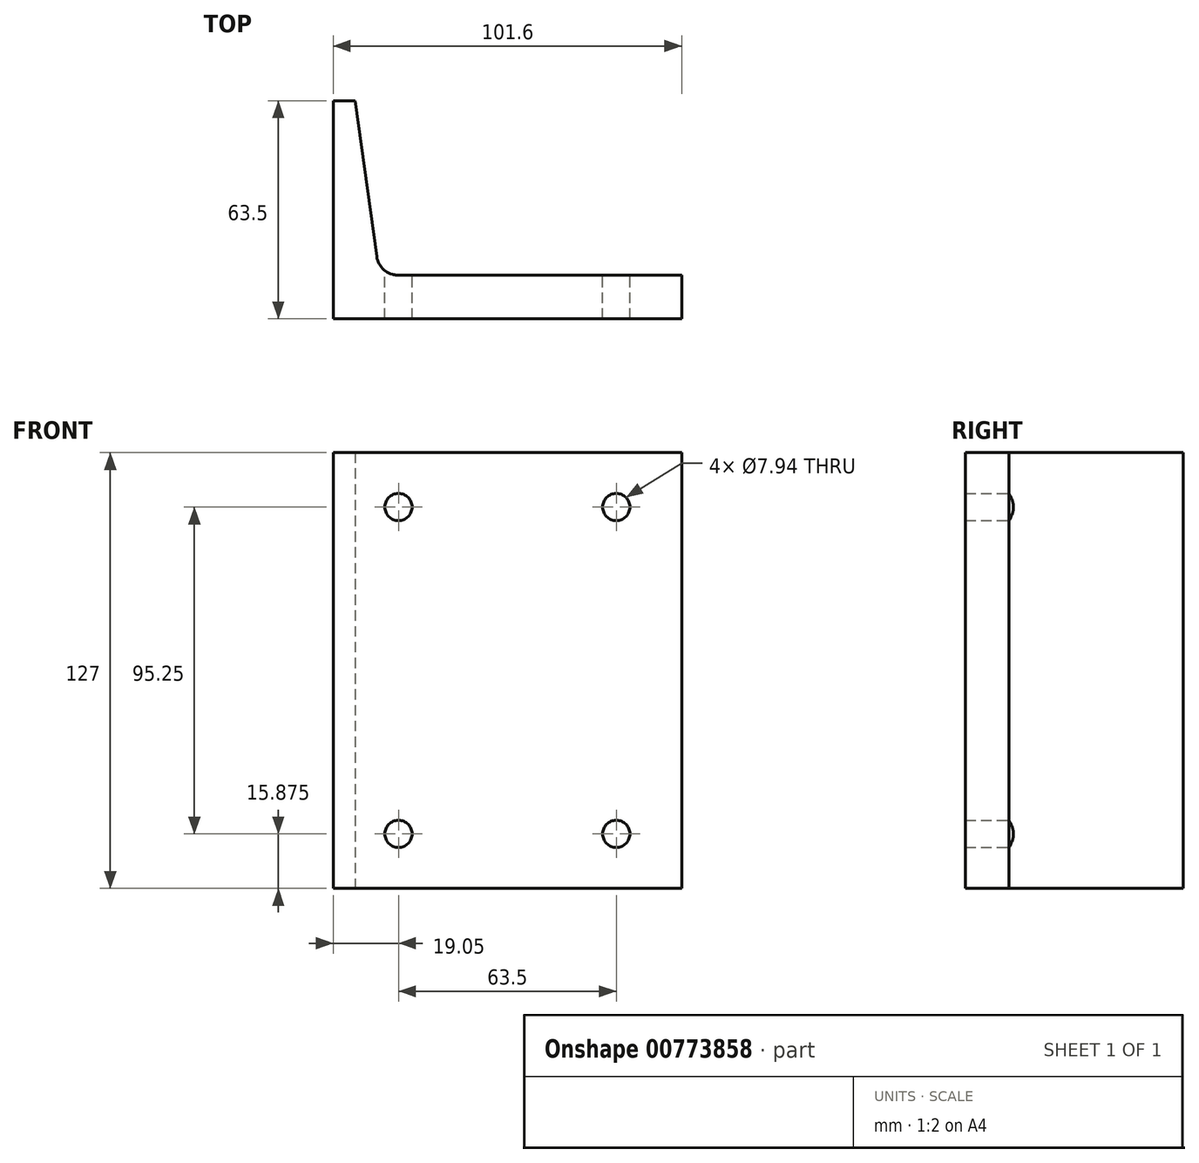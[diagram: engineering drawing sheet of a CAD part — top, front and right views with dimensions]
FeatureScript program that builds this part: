
annotation { "Feature Type Name" : "Feature", "Feature Type Description" : "" }
export const myFeature = defineFeature(function(context is Context, id is Id, definition is map)
    precondition{}
    {
        {
            var Q0;
            Q0=qCreatedBy(makeId("Top.planeOp"),FACE);
            var sketch = newSketch(context, id + "F0", { "sketchPlane" : qUnion([Q0])});
            skLineSegment(sketch, "E0", {"start": v(0, 0) * mm, "end": v(0, 63.5) * mm});
            skLineSegment(sketch, "E1", {"start": v(0, 63.5) * mm, "end": v(6.35, 63.5) * mm});
            skLineSegment(sketch, "E2", {"start": v(6.35, 63.5) * mm, "end": v(12.7, 18.17) * mm});
            skLineSegment(sketch, "E3", {"start": v(18.99, 12.7) * mm, "end": v(101.6, 12.7) * mm});
            skLineSegment(sketch, "E4", {"start": v(101.6, 12.7) * mm, "end": v(101.6, 0) * mm});
            skLineSegment(sketch, "E5", {"start": v(101.6, 0) * mm, "end": v(0, 0) * mm});
            skArc(sketch, "E6.filletArc", {"start": v(12.7, 18.17) * mm, "mid": v(14.82, 14.26) * mm, "end": v(18.99, 12.7) * mm});
            skSolve(sketch);
        }
        {
            var Q0;
            Q0 = qSketchRegion(id + "F0", true);
            extrude(context, id + "F1", {"entities" : qUnion([Q0]), "depth" : 127 * mm, "offsetDistance" : 25.4 * mm});
        }
        {
            var Q0;
            Q0=makeQuery(id+"F1.opExtrude","SWEPT_FACE",FACE,{"disambiguationData":[OSD([sQuery(id+"F0.wireOp",EDGE,"E5")])]});
            var sketch = newSketch(context, id + "F2", { "sketchPlane" : qUnion([Q0])});
            skPoint(sketch, "E7", {"position": v(19.05, 111.13) * mm});
            skPoint(sketch, "E8", {"position": v(82.55, 111.13) * mm});
            skPoint(sketch, "E9", {"position": v(82.55, 15.88) * mm});
            skPoint(sketch, "E10", {"position": v(19.05, 15.88) * mm});
            skSolve(sketch);
        }
        {
            var Q0;
            Q0=sQuery(id+"F2.wireOp",VERTEX,"E7");
            var Q1;
            Q1=sQuery(id+"F2.wireOp",VERTEX,"E8");
            var Q2;
            Q2=sQuery(id+"F2.wireOp",VERTEX,"E9");
            var Q3;
            Q3=sQuery(id+"F2.wireOp",VERTEX,"E10");
            var Q4;
            Q4=makeQuery(id+"F1.opExtrude","SWEPT_BODY",BODY,{"disambiguationData":[OSD([sQuery(id+"F0.wireOp",EDGE,"E0"),sQuery(id+"F0.wireOp",EDGE,"E1"),sQuery(id+"F0.wireOp",EDGE,"E2"),sQuery(id+"F0.wireOp",EDGE,"E3"),sQuery(id+"F0.wireOp",EDGE,"E4"),sQuery(id+"F0.wireOp",EDGE,"E5"),sQuery(id+"F0.wireOp",EDGE,"E6.filletArc")])]});
            hole(context, id + "F3", {"style" : HoleStyle.SIMPLE, "endStyle" : HoleEndStyle.BLIND, "standardTappedOrClearance" : lookupTablePath({ "standard" : "ANSI", "engagement" : "75%", "pitch" : "16 tpi", "size" : "3/8", "type" : "Tapped" }), "standardBlindInLast" : lookupTablePath({ "standard" : "ANSI", "fit" : "Free", "engagement" : "75%", "pitch" : "16 tpi", "size" : "3/8", "type" : "Clearance & tapped" }), "holeDiameter" : 7.94 * mm, "majorDiameter" : 9.52 * mm, "showTappedDepth" : true, "holeDepth" : 17.46 * mm, "tappedDepth" : 12.7 * mm, "tapClearance" : 3, "locations" : qUnion([Q0, Q1, Q2, Q3]), "scope" : qUnion([Q4])});
        }
    });
